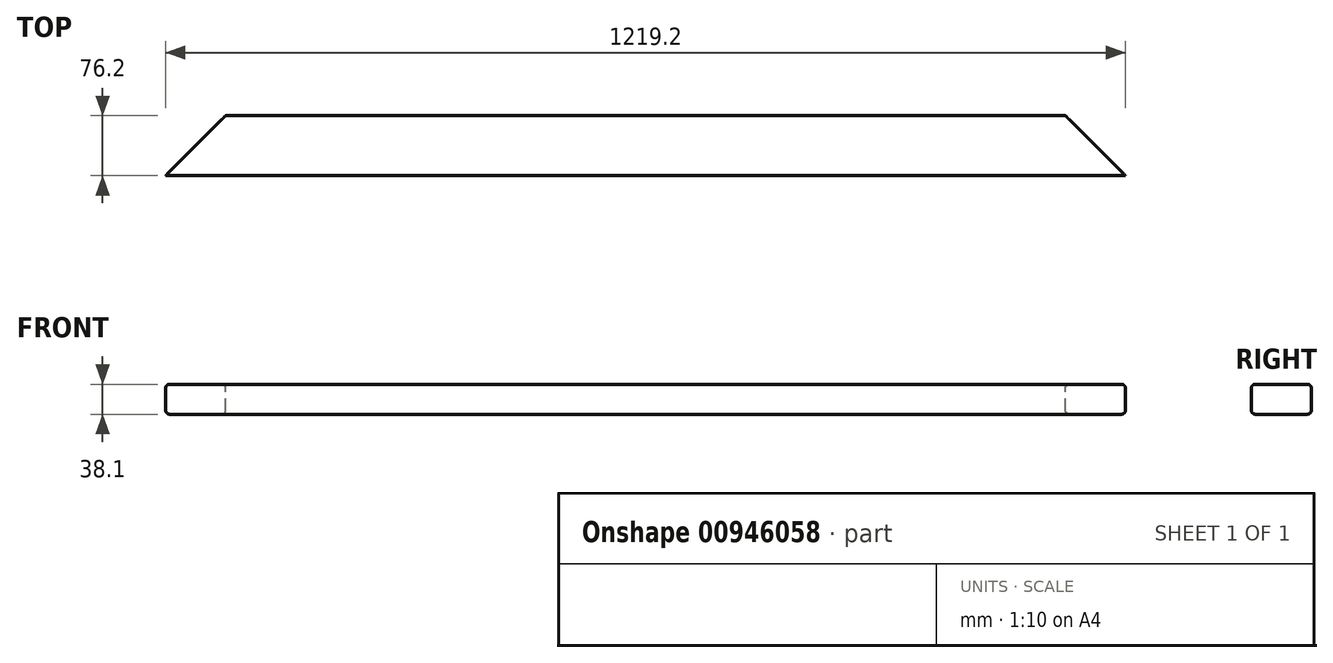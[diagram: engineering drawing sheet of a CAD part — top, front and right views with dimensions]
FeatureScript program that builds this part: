
annotation { "Feature Type Name" : "Feature", "Feature Type Description" : "" }
export const myFeature = defineFeature(function(context is Context, id is Id, definition is map)
    precondition{}
    {
        {
            var Q0;
            Q0=qCreatedBy(makeId("Top.planeOp"),FACE);
            var sketch = newSketch(context, id + "F0", { "sketchPlane" : qUnion([Q0])});
            skLineSegment(sketch, "E0.bottom", {"start": v(-609.6, 38.1) * mm, "end": v(609.6, 38.1) * mm});
            skLineSegment(sketch, "E0.top", {"start": v(-609.6, -38.1) * mm, "end": v(609.6, -38.1) * mm});
            skLineSegment(sketch, "E0.left", {"start": v(-609.6, 38.1) * mm, "end": v(-609.6, -38.1) * mm});
            skLineSegment(sketch, "E0.right", {"start": v(609.6, 38.1) * mm, "end": v(609.6, -38.1) * mm});
            skSolve(sketch);
        }
        {
            var Q0;
            Q0=makeQuery(id+"F0.imprint","IMPRINT",FACE,{"disambiguationData":[TD([[makeQuery(id+"F0.imprint","IMPRINT",EDGE,{"derivedFrom":sQuery(id+"F0.wireOp",EDGE,"E0.bottom")}),-1.0]])]});
            extrude(context, id + "F1", {"entities" : qUnion([Q0]), "depth" : 38.1 * mm, "offsetDistance" : 25.4 * mm});
        }
        {
            var Q0;
            Q0=makeQuery(id+"F1.opExtrude","CAP_FACE",FACE,{"disambiguationData":[OSD([sQuery(id+"F0.wireOp",EDGE,"E0.bottom"),sQuery(id+"F0.wireOp",EDGE,"E0.top"),sQuery(id+"F0.wireOp",EDGE,"E0.left"),sQuery(id+"F0.wireOp",EDGE,"E0.right")])],"isStart":false});
            var sketch = newSketch(context, id + "F2", { "sketchPlane" : qUnion([Q0])});
            skLineSegment(sketch, "E1", {"start": v(-609.6, -38.1) * mm, "end": v(-533.4, 38.1) * mm});
            skLineSegment(sketch, "E2", {"start": v(0, -38.1) * mm, "end": v(0, 38.1) * mm, "construction": true});
            skLineSegment(sketch, "E3.MirrorCS", {"start": v(609.6, -38.1) * mm, "end": v(533.4, 38.1) * mm});
            skSolve(sketch);
        }
        {
            var Q0;
            {var subQ0=sQuery(id+"F2.wireOp",EDGE,"E1");Q0=makeQuery(id+"F2.imprint","IMPRINT",FACE,{"disambiguationData":[TD([[makeQuery(id+"F2.imprint","IMPRINT",EDGE,{"derivedFrom":subQ0}),1.0]])]});}
            var Q1;
            {var subQ0=sQuery(id+"F2.wireOp",EDGE,"E3.MirrorCS");Q1=makeQuery(id+"F2.imprint","IMPRINT",FACE,{"disambiguationData":[TD([[makeQuery(id+"F2.imprint","IMPRINT",EDGE,{"derivedFrom":subQ0}),-1.0]])]});}
            extrude(context, id + "F3", {"entities" : qUnion([Q0, Q1]), "operationType" : NewBodyOperationType.REMOVE, "endBound" : BoundingType.THROUGH_ALL, "oppositeDirection" : true, "depth" : 25.4 * mm, "offsetDistance" : 25.4 * mm});
        }
        {
            var Q0;
            Q0=makeQuery(id+"F1.opExtrude","CAP_EDGE",EDGE,{"disambiguationData":[OSD([sQuery(id+"F0.wireOp",EDGE,"E0.bottom")])],"isStart":true});
            var Q1;
            Q1=makeQuery(id+"F1.opExtrude","CAP_EDGE",EDGE,{"disambiguationData":[OSD([sQuery(id+"F0.wireOp",EDGE,"E0.top")])],"isStart":true});
            var Q2;
            Q2=makeQuery(id+"F1.opExtrude","CAP_EDGE",EDGE,{"disambiguationData":[OSD([sQuery(id+"F0.wireOp",EDGE,"E0.top")])],"isStart":false});
            var Q3;
            Q3=makeQuery(id+"F1.opExtrude","CAP_EDGE",EDGE,{"disambiguationData":[OSD([sQuery(id+"F0.wireOp",EDGE,"E0.bottom")])],"isStart":false});
            fillet(context, id + "F4", {"entities" : qUnion([Q0, Q1, Q2, Q3]), "radius" : 5.08 * mm, "tangentPropagation" : true, "allowEdgeOverflow" : false});
        }
    });
